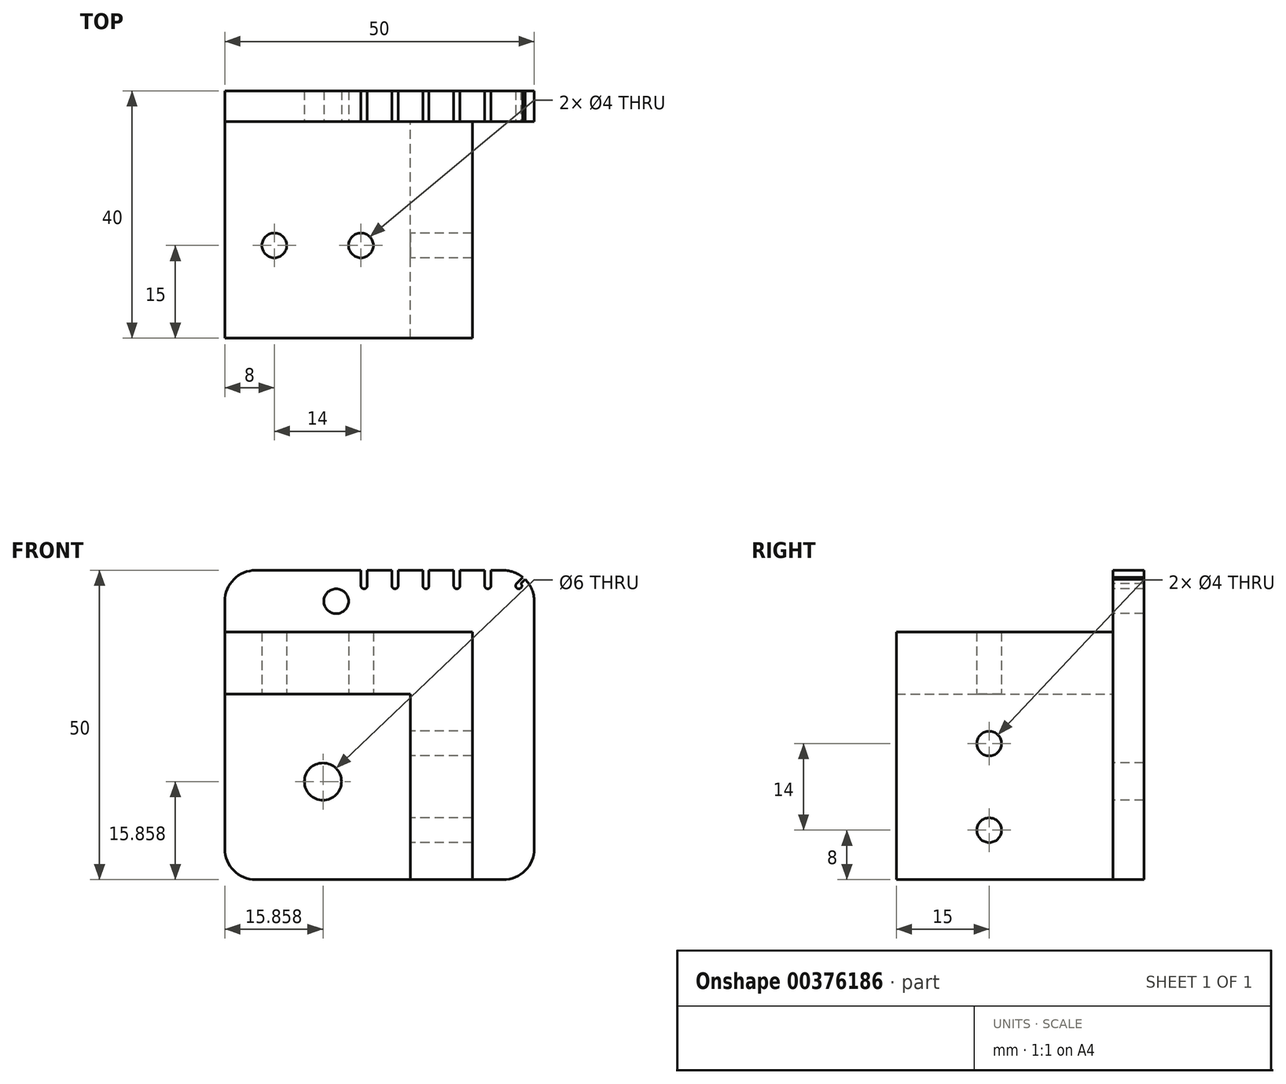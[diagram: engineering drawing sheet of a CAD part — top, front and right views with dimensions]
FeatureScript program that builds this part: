
annotation { "Feature Type Name" : "Feature", "Feature Type Description" : "" }
export const myFeature = defineFeature(function(context is Context, id is Id, definition is map)
    precondition{}
    {
        {
            assignVariable(context, id + "F0", {"name" : "P", "anyValue" : 5 * mm});
        }
        {
            var Q0;
            Q0=qCreatedBy(makeId("Front.planeOp"),FACE);
            var sketch = newSketch(context, id + "F1", { "sketchPlane" : qUnion([Q0])});
            skLineSegment(sketch, "E0", {"start": v(0, 0) * mm, "end": v(-40, 0) * mm});
            skLineSegment(sketch, "E1", {"start": v(-40, -10) * mm, "end": v(-10, -10) * mm});
            skLineSegment(sketch, "E2", {"start": v(-40, 10) * mm, "end": v(10, 10) * mm});
            skLineSegment(sketch, "E3", {"start": v(-40, 7.5) * mm, "end": v(10, 7.5) * mm});
            skPoint(sketch, "E4", {"position": v(-2.5, 7.5) * mm});
            skPoint(sketch, "E5", {"position": v(-7.5, 7.5) * mm});
            skPoint(sketch, "E6", {"position": v(-12.5, 7.5) * mm});
            skPoint(sketch, "E7", {"position": v(2.5, 7.5) * mm});
            skLineSegment(sketch, "E8", {"start": v(-40, -40) * mm, "end": v(10, 10) * mm});
            skLineSegment(sketch, "E9", {"start": v(-40, -40) * mm, "end": v(10, -40) * mm});
            skLineSegment(sketch, "E10", {"start": v(10, -40) * mm, "end": v(10, 10) * mm});
            skLineSegment(sketch, "E11", {"start": v(-40, 10) * mm, "end": v(-40, -40) * mm});
            skLineSegment(sketch, "E12", {"start": v(0, 0) * mm, "end": v(0, -40) * mm});
            skLineSegment(sketch, "E13", {"start": v(-10, -10) * mm, "end": v(-10, -40) * mm});
            skLineSegment(sketch, "E14.MirrorCS", {"start": v(7.5, -40) * mm, "end": v(7.5, 10) * mm});
            skPoint(sketch, "E15", {"position": v(-17.5, 7.5) * mm});
            skPoint(sketch, "E16", {"position": v(7.5, 7.5) * mm});
            skLineSegment(sketch, "E17", {"start": v(-40, 5) * mm, "end": v(10, 5) * mm});
            skSolve(sketch);
        }
        {
            var Q0;
            {var subQ0=sQuery(id+"F1.wireOp",EDGE,"E0");Q0=makeQuery(id+"F1.imprint","IMPRINT",FACE,{"disambiguationData":[TD([[makeQuery(id+"F1.imprint","IMPRINT",EDGE,{"derivedFrom":subQ0}),-1.0]])]});}
            var Q1;
            {var subQ0=sQuery(id+"F1.wireOp",EDGE,"E0");Q1=makeQuery(id+"F1.imprint","IMPRINT",FACE,{"disambiguationData":[TD([[makeQuery(id+"F1.imprint","IMPRINT",EDGE,{"derivedFrom":subQ0}),1.0]])]});}
            var Q2;
            {var subQ1=sQuery(id+"F1.wireOp",EDGE,"E2");var subQ3=sQuery(id+"F1.wireOp",EDGE,"E14.MirrorCS");var subQ4=makeQuery(id+"F1.imprint","INTERSECT",VERTEX,{"derivedFrom":[subQ1,subQ3]});Q2=makeQuery(id+"F1.imprint","IMPRINT",FACE,{"disambiguationData":[TD([[makeQuery(id+"F1.imprint","IMPRINT",EDGE,{"disambiguationData":[TD([[subQ4,-1.0]])],"derivedFrom":subQ1}),-1.0]])]});}
            var Q3;
            {var subQ0=sQuery(id+"F1.wireOp",EDGE,"E11");var subQ1=sQuery(id+"F1.wireOp",EDGE,"E2");var subQ2=makeQuery(id+"F1.imprint","INTERSECT",VERTEX,{"derivedFrom":[subQ1,subQ0]});Q3=makeQuery(id+"F1.imprint","IMPRINT",FACE,{"disambiguationData":[TD([[makeQuery(id+"F1.imprint","IMPRINT",EDGE,{"disambiguationData":[TD([[subQ2,-1.0]])],"derivedFrom":subQ1}),-1.0]])]});}
            var Q4;
            {var subQ0=sQuery(id+"F1.wireOp",EDGE,"E13");Q4=makeQuery(id+"F1.imprint","IMPRINT",FACE,{"disambiguationData":[TD([[makeQuery(id+"F1.imprint","IMPRINT",EDGE,{"derivedFrom":subQ0}),-1.0]])]});}
            var Q5;
            {var subQ0=sQuery(id+"F1.wireOp",EDGE,"E1");Q5=makeQuery(id+"F1.imprint","IMPRINT",FACE,{"disambiguationData":[TD([[makeQuery(id+"F1.imprint","IMPRINT",EDGE,{"derivedFrom":subQ0}),-1.0]])]});}
            var Q6;
            {var subQ0=sQuery(id+"F1.wireOp",EDGE,"E10");var subQ1=sQuery(id+"F1.wireOp",EDGE,"E3");var subQ2=makeQuery(id+"F1.imprint","INTERSECT",VERTEX,{"derivedFrom":[subQ1,subQ0]});Q6=makeQuery(id+"F1.imprint","IMPRINT",FACE,{"disambiguationData":[TD([[makeQuery(id+"F1.imprint","IMPRINT",EDGE,{"disambiguationData":[TD([[subQ2,1.0]])],"derivedFrom":subQ1}),1.0]])]});}
            var Q7;
            {var subQ0=sQuery(id+"F1.wireOp",EDGE,"E12");Q7=makeQuery(id+"F1.imprint","IMPRINT",FACE,{"disambiguationData":[TD([[makeQuery(id+"F1.imprint","IMPRINT",EDGE,{"derivedFrom":subQ0}),-1.0]])]});}
            var Q8;
            {var subQ0=sQuery(id+"F1.wireOp",EDGE,"E12");Q8=makeQuery(id+"F1.imprint","IMPRINT",FACE,{"disambiguationData":[TD([[makeQuery(id+"F1.imprint","IMPRINT",EDGE,{"derivedFrom":subQ0}),1.0]])]});}
            var Q9;
            {var subQ0=sQuery(id+"F1.wireOp",EDGE,"E10");var subQ5=sQuery(id+"F1.wireOp",EDGE,"E9");var subQ6=makeQuery(id+"F1.imprint","INTERSECT",VERTEX,{"derivedFrom":[subQ5,subQ0]});Q9=makeQuery(id+"F1.imprint","IMPRINT",FACE,{"disambiguationData":[TD([[makeQuery(id+"F1.imprint","IMPRINT",EDGE,{"disambiguationData":[TD([[subQ6,1.0]])],"derivedFrom":subQ5}),1.0]])]});}
            var Q10;
            {var subQ0=sQuery(id+"F1.wireOp",EDGE,"E11");var subQ1=sQuery(id+"F1.wireOp",EDGE,"E3");var subQ2=makeQuery(id+"F1.imprint","INTERSECT",VERTEX,{"derivedFrom":[subQ1,subQ0]});Q10=makeQuery(id+"F1.imprint","IMPRINT",FACE,{"disambiguationData":[TD([[makeQuery(id+"F1.imprint","IMPRINT",EDGE,{"disambiguationData":[TD([[subQ2,-1.0]])],"derivedFrom":subQ0}),1.0]])]});}
            var Q11;
            {var subQ0=sQuery(id+"F1.wireOp",EDGE,"E17");var subQ1=sQuery(id+"F1.wireOp",EDGE,"E8");var subQ2=makeQuery(id+"F1.imprint","INTERSECT",VERTEX,{"derivedFrom":[subQ1,subQ0]});Q11=makeQuery(id+"F1.imprint","IMPRINT",FACE,{"disambiguationData":[TD([[makeQuery(id+"F1.imprint","IMPRINT",EDGE,{"disambiguationData":[TD([[subQ2,-1.0]])],"derivedFrom":subQ0}),1.0]])]});}
            var Q12;
            {var subQ0=sQuery(id+"F1.wireOp",EDGE,"E10");var subQ1=sQuery(id+"F1.wireOp",EDGE,"E3");var subQ2=makeQuery(id+"F1.imprint","INTERSECT",VERTEX,{"derivedFrom":[subQ1,subQ0]});Q12=makeQuery(id+"F1.imprint","IMPRINT",FACE,{"disambiguationData":[TD([[makeQuery(id+"F1.imprint","IMPRINT",EDGE,{"disambiguationData":[TD([[subQ2,1.0]])],"derivedFrom":subQ0}),1.0]])]});}
            extrude(context, id + "F2", {"entities" : qUnion([Q0, Q1, Q2, Q3, Q4, Q5, Q6, Q7, Q8, Q9, Q10, Q11, Q12]), "oppositeDirection" : true, "depth" : getVariable(context, 'P')});
        }
        {
            var Q0;
            Q0=makeQuery(id+"F2.opExtrude","SWEPT_EDGE",EDGE,{"disambiguationData":[OSD([sQuery(id+"F1.wireOp",EDGE,"E9"),sQuery(id+"F1.wireOp",EDGE,"E10")])]});
            var Q1;
            Q1=makeQuery(id+"F2.opExtrude","SWEPT_EDGE",EDGE,{"disambiguationData":[OSD([sQuery(id+"F1.wireOp",EDGE,"E2"),sQuery(id+"F1.wireOp",EDGE,"E8"),sQuery(id+"F1.wireOp",EDGE,"E10")])]});
            var Q2;
            Q2=makeQuery(id+"F2.opExtrude","SWEPT_EDGE",EDGE,{"disambiguationData":[OSD([sQuery(id+"F1.wireOp",EDGE,"E2"),sQuery(id+"F1.wireOp",EDGE,"E11")])]});
            var Q3;
            Q3=makeQuery(id+"F2.opExtrude","SWEPT_EDGE",EDGE,{"disambiguationData":[OSD([sQuery(id+"F1.wireOp",EDGE,"E8"),sQuery(id+"F1.wireOp",EDGE,"E9"),sQuery(id+"F1.wireOp",EDGE,"E11")])]});
            fillet(context, id + "F3", {"entities" : qUnion([Q0, Q1, Q2, Q3]), "radius" : 5 * mm, "tangentPropagation" : true, "allowEdgeOverflow" : false});
        }
        {
            var Q0;
            Q0=makeQuery(id+"F1.imprint","IMPRINT",FACE,{"disambiguationData":[TD([[makeQuery(id+"F1.imprint","IMPRINT",EDGE,{"derivedFrom":sQuery(id+"F1.wireOp",EDGE,"E0")}),-1.0]])]});
            var sketch = newSketch(context, id + "F4", { "sketchPlane" : qUnion([Q0])});
            skLineSegment(sketch, "E18.0", {"start": v(-40, 10) * mm, "end": v(10, 10) * mm});
            skPoint(sketch, "E19.0", {"position": v(2.5, 7.5) * mm});
            skPoint(sketch, "E20.0", {"position": v(-2.5, 7.5) * mm});
            skPoint(sketch, "E21.0", {"position": v(-7.5, 7.5) * mm});
            skPoint(sketch, "E22.0", {"position": v(-12.5, 7.5) * mm});
            skCircle(sketch, "E23", {"center": v(2.5, 7.5) * mm, "radius": 0.5 * mm});
            skLineSegment(sketch, "E24", {"start": v(3, 7.5) * mm, "end": v(3, 10) * mm});
            skLineSegment(sketch, "E25", {"start": v(2, 7.5) * mm, "end": v(2, 10) * mm});
            skCircle(sketch, "E26", {"center": v(-2.5, 7.5) * mm, "radius": 0.5 * mm});
            skLineSegment(sketch, "E27", {"start": v(-2, 7.5) * mm, "end": v(-2, 10) * mm});
            skLineSegment(sketch, "E28", {"start": v(-3, 7.5) * mm, "end": v(-3, 10) * mm});
            skCircle(sketch, "E29", {"center": v(-7.5, 7.5) * mm, "radius": 0.5 * mm});
            skLineSegment(sketch, "E30", {"start": v(-7, 7.5) * mm, "end": v(-7, 10) * mm});
            skLineSegment(sketch, "E31", {"start": v(-8, 7.5) * mm, "end": v(-8, 10) * mm});
            skCircle(sketch, "E32", {"center": v(-12.5, 7.5) * mm, "radius": 0.5 * mm});
            skLineSegment(sketch, "E33", {"start": v(-12, 7.5) * mm, "end": v(-12, 10) * mm});
            skLineSegment(sketch, "E34", {"start": v(-13, 7.5) * mm, "end": v(-13, 10) * mm});
            skPoint(sketch, "E35.0", {"position": v(-17.5, 7.5) * mm});
            skCircle(sketch, "E36", {"center": v(-17.5, 7.5) * mm, "radius": 0.5 * mm});
            skLineSegment(sketch, "E37", {"start": v(-17, 7.5) * mm, "end": v(-17, 10) * mm});
            skLineSegment(sketch, "E38", {"start": v(-18, 7.5) * mm, "end": v(-18, 10) * mm});
            skPoint(sketch, "E39.0", {"position": v(7.5, 7.5) * mm});
            skCircle(sketch, "E40", {"center": v(7.5, 7.5) * mm, "radius": 0.5 * mm});
            skLineSegment(sketch, "E41", {"start": v(7.15, 7.85) * mm, "end": v(9.3, 10) * mm});
            skLineSegment(sketch, "E42", {"start": v(7.5, 7.5) * mm, "end": v(10, 10) * mm});
            skSolve(sketch);
        }
        {
            var Q0;
            Q0=qSketchRegion(id+"F4",true);
            extrude(context, id + "F5", {"entities" : qUnion([Q0]), "operationType" : NewBodyOperationType.REMOVE, "oppositeDirection" : true, "depth" : 25 * mm});
        }
        {
            var Q0;
            Q0=makeQuery(id+"F1.imprint","IMPRINT",FACE,{"disambiguationData":[TD([[makeQuery(id+"F1.imprint","IMPRINT",EDGE,{"derivedFrom":sQuery(id+"F1.wireOp",EDGE,"E0")}),1.0]])]});
            extrude(context, id + "F6", {"entities" : qUnion([Q0]), "depth" : 35 * mm});
        }
        {
            var Q0;
            Q0=makeQuery(id+"F6.opExtrude","SWEPT_FACE",FACE,{"disambiguationData":[OSD([sQuery(id+"F1.wireOp",EDGE,"E1")])]});
            var sketch = newSketch(context, id + "F7", { "sketchPlane" : qUnion([Q0])});
            skLineSegment(sketch, "E43", {"start": v(-32, 20) * mm, "end": v(-18, 20) * mm, "construction": true});
            skSolve(sketch);
        }
        {
            var Q0;
            Q0=makeQuery(id+"F1.imprint","IMPRINT",FACE,{"disambiguationData":[TD([[makeQuery(id+"F1.imprint","IMPRINT",EDGE,{"derivedFrom":sQuery(id+"F1.wireOp",EDGE,"E0")}),-1.0]])]});
            var sketch = newSketch(context, id + "F8", { "sketchPlane" : qUnion([Q0])});
            skLineSegment(sketch, "E44.0", {"start": v(-40, 5) * mm, "end": v(10, 5) * mm});
            skPoint(sketch, "E45", {"position": v(-22, 5) * mm});
            skSolve(sketch);
        }
        {
            var Q0;
            Q0=sQuery(id+"F8.wireOp",VERTEX,"E45");
            var Q1;
            Q1=sQuery(id+"F7.wireOp",VERTEX,"E43.start");
            var Q2;
            Q2=sQuery(id+"F7.wireOp",VERTEX,"E43.end");
            var Q3;
            Q3=makeQuery(id+"F2.opExtrude","SWEPT_BODY",BODY,{"disambiguationData":[OSD([sQuery(id+"F1.wireOp",EDGE,"1DaqamyI-7lqo-KkOJ-ihTs-gG18izMV09v4"),sQuery(id+"F1.wireOp",EDGE,"M4KmeI0G-XzYf-h7ro-I2hb-yDohJINmiRMZ"),sQuery(id+"F1.wireOp",EDGE,"E2"),sQuery(id+"F1.wireOp",EDGE,"lPCfZZdf-uFaS-SMpN-JuiH-cfmB2BQoF5xf"),sQuery(id+"F1.wireOp",EDGE,"uaqze6CX-x6As-Z0uJ-E2p3-aBXWaqMbbjSt")])]});
            var Q4;
            Q4=makeQuery(id+"F6.opExtrude","SWEPT_BODY",BODY,{"disambiguationData":[OSD([sQuery(id+"F1.wireOp",EDGE,"E0"),sQuery(id+"F1.wireOp",EDGE,"4cMmOav8-hxjt-aCIH-ei5P-ZmF8k5vxPAVi"),sQuery(id+"F1.wireOp",EDGE,"KMjolukR-kPRg-Pcgj-MXfF-0PXWrHXV2e2y"),sQuery(id+"F1.wireOp",EDGE,"E1"),sQuery(id+"F1.wireOp",EDGE,"zInli9W6-7XTx-WogI-O8dR-9fGRW67Pu5JT"),sQuery(id+"F1.wireOp",EDGE,"uaqze6CX-x6As-Z0uJ-E2p3-aBXWaqMbbjSt")])]});
            hole(context, id + "F9", {"style" : HoleStyle.SIMPLE, "endStyle" : HoleEndStyle.THROUGH, "holeDiameter" : 4 * mm, "tappedDepth" : 12 * mm, "tapClearance" : 3, "locations" : qUnion([Q0, Q1, Q2]), "scope" : qUnion([Q3, Q4])});
        }
        {
            var Q0;
            Q0=makeQuery(id+"F2.opExtrude","CAP_FACE",FACE,{"disambiguationData":[OSD([sQuery(id+"F1.wireOp",EDGE,"E2"),sQuery(id+"F1.wireOp",EDGE,"E9"),sQuery(id+"F1.wireOp",EDGE,"E10"),sQuery(id+"F1.wireOp",EDGE,"E11")])],"isStart":true});
            var sketch = newSketch(context, id + "F10", { "sketchPlane" : qUnion([Q0])});
            skLineSegment(sketch, "E46.0", {"start": v(-40, -10) * mm, "end": v(-10, -10) * mm});
            skPoint(sketch, "E47", {"position": v(13.21, 13.21) * mm});
            skLineSegment(sketch, "E48.0", {"start": v(-40, -40) * mm, "end": v(10, 10) * mm});
            skPoint(sketch, "E49", {"position": v(-24.14, -24.14) * mm});
            skSolve(sketch);
        }
        {
            var Q0;
            Q0=sQuery(id+"F10.wireOp",VERTEX,"E49");
            var Q1;
            Q1=makeQuery(id+"F2.opExtrude","SWEPT_BODY",BODY,{"disambiguationData":[OSD([sQuery(id+"F1.wireOp",EDGE,"1DaqamyI-7lqo-KkOJ-ihTs-gG18izMV09v4"),sQuery(id+"F1.wireOp",EDGE,"M4KmeI0G-XzYf-h7ro-I2hb-yDohJINmiRMZ"),sQuery(id+"F1.wireOp",EDGE,"E2"),sQuery(id+"F1.wireOp",EDGE,"lPCfZZdf-uFaS-SMpN-JuiH-cfmB2BQoF5xf"),sQuery(id+"F1.wireOp",EDGE,"uaqze6CX-x6As-Z0uJ-E2p3-aBXWaqMbbjSt")])]});
            hole(context, id + "F11", {"style" : HoleStyle.SIMPLE, "endStyle" : HoleEndStyle.THROUGH, "holeDiameter" : 6 * mm, "isTappedThrough" : true, "tappedDepth" : 35 * mm, "tapClearance" : 3, "startFromSketch" : true, "locations" : qUnion([Q0]), "scope" : qUnion([Q1])});
        }
        {
            var Q0;
            Q0=makeQuery(id+"F6.opExtrude","SWEPT_BODY",BODY,{"disambiguationData":[OSD([sQuery(id+"F1.wireOp",EDGE,"E0"),sQuery(id+"F1.wireOp",EDGE,"E1"),sQuery(id+"F1.wireOp",EDGE,"E8"),sQuery(id+"F1.wireOp",EDGE,"E11")])]});
            var Q1;
            Q1=makeQuery(id+"F6.opExtrude","SWEPT_FACE",FACE,{"disambiguationData":[OSD([sQuery(id+"F1.wireOp",EDGE,"E8")])]});
            mirror(context, id + "F12", {"operationType" : NewBodyOperationType.ADD, "entities" : qUnion([Q0]), "mirrorPlane" : qUnion([Q1])});
        }
    });
